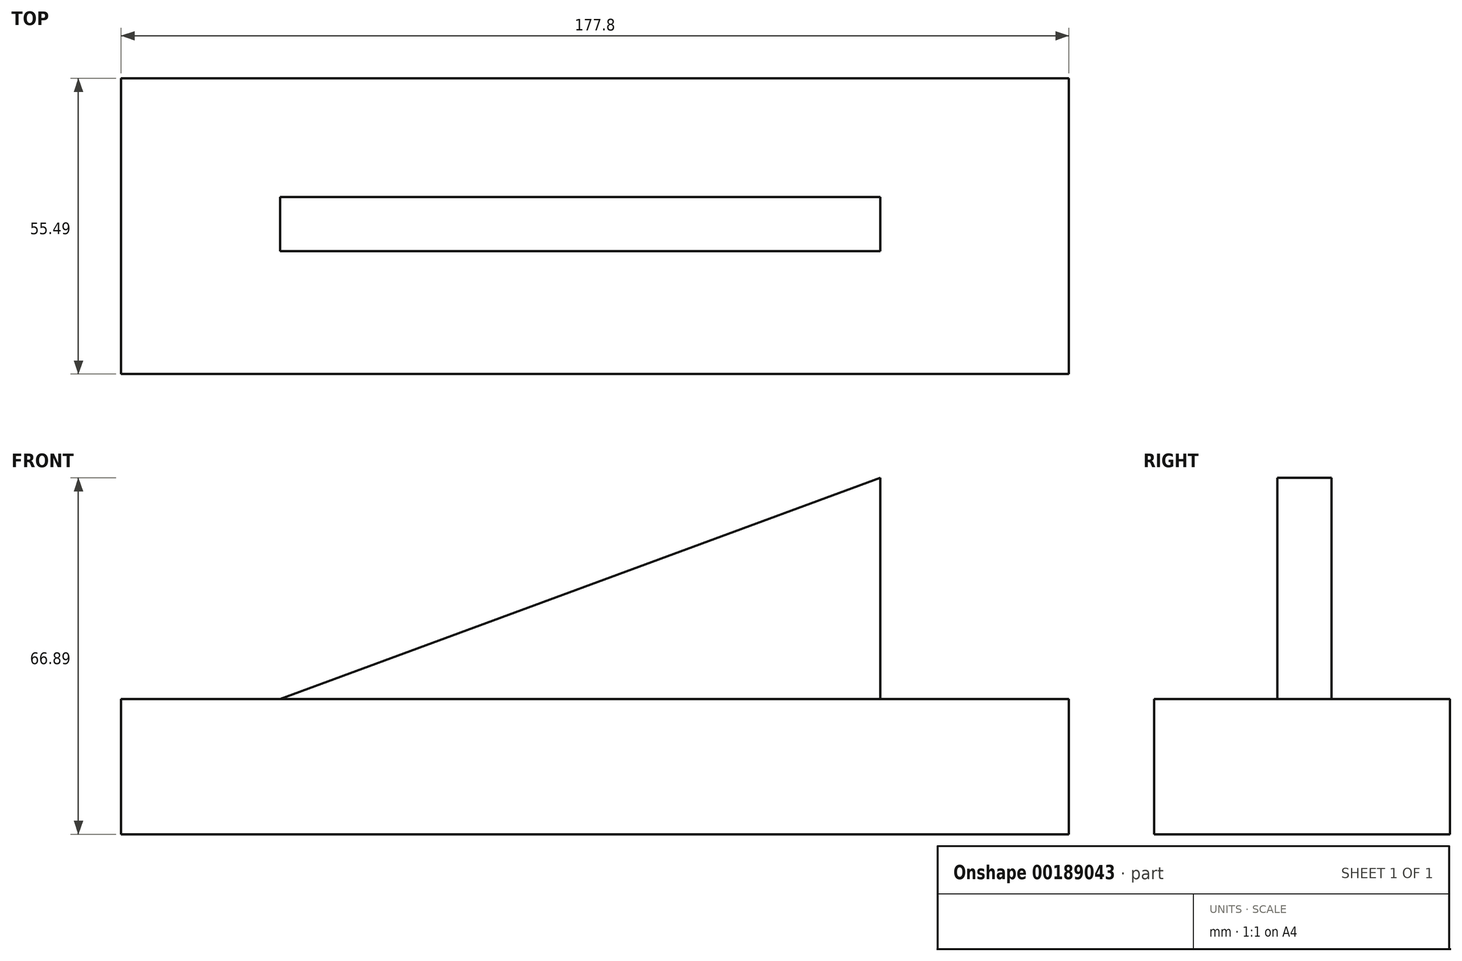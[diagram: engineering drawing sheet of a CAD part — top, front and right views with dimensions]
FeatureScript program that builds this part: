
annotation { "Feature Type Name" : "Feature", "Feature Type Description" : "" }
export const myFeature = defineFeature(function(context is Context, id is Id, definition is map)
    precondition{}
    {
        {
            var Q0;
            Q0=qCreatedBy(makeId("Top.planeOp"),FACE);
            var sketch = newSketch(context, id + "F0", { "sketchPlane" : qUnion([Q0])});
            skLineSegment(sketch, "E0.bottom", {"start": v(-88.3, 24.8) * mm, "end": v(89.5, 24.8) * mm});
            skLineSegment(sketch, "E0.top", {"start": v(-88.3, -30.7) * mm, "end": v(89.5, -30.7) * mm});
            skLineSegment(sketch, "E0.left", {"start": v(-88.3, 24.8) * mm, "end": v(-88.3, -30.7) * mm});
            skLineSegment(sketch, "E0.right", {"start": v(89.5, 24.8) * mm, "end": v(89.5, -30.7) * mm});
            skSolve(sketch);
        }
        {
            var Q0;
            Q0 = qSketchRegion(id + "F0", true);
            extrude(context, id + "F1", {"entities" : qUnion([Q0]), "depth" : 25.4 * mm});
        }
        {
            var Q0;
            Q0=qCreatedBy(makeId("Front.planeOp"),FACE);
            var sketch = newSketch(context, id + "F2", { "sketchPlane" : qUnion([Q0])});
            skLineSegment(sketch, "E1", {"start": v(-58.63, 25.35) * mm, "end": v(54.12, 66.89) * mm});
            skLineSegment(sketch, "E2", {"start": v(54.12, 66.89) * mm, "end": v(54.12, 25.08) * mm});
            skLineSegment(sketch, "E3", {"start": v(54.12, 25.08) * mm, "end": v(-58.63, 25.35) * mm});
            skSolve(sketch);
        }
        {
            var Q0;
            Q0 = qSketchRegion(id + "F2", true);
            extrude(context, id + "F3", {"entities" : qUnion([Q0]), "operationType" : NewBodyOperationType.ADD, "depth" : 7.62 * mm, "hasSecondDirection" : true, "secondDirectionOppositeDirection" : true, "secondDirectionDepth" : 2.54 * mm});
        }
    });
